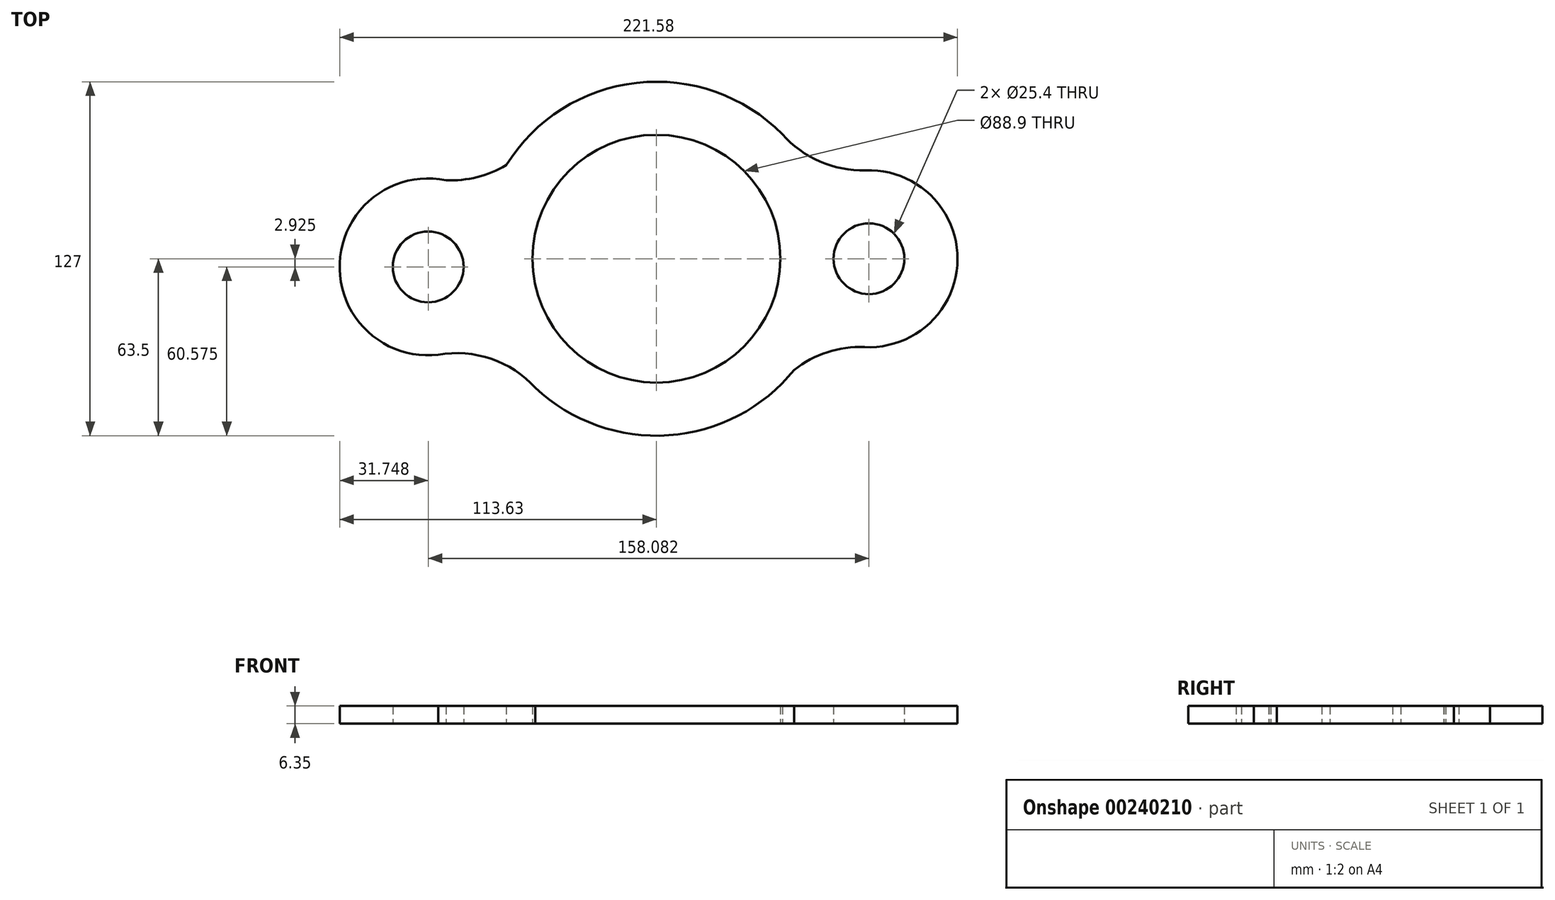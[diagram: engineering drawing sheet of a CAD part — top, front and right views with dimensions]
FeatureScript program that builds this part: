
annotation { "Feature Type Name" : "Feature", "Feature Type Description" : "" }
export const myFeature = defineFeature(function(context is Context, id is Id, definition is map)
    precondition{}
    {
        {
            var Q0;
            Q0=qCreatedBy(makeId("Top.planeOp"),FACE);
            var sketch = newSketch(context, id + "F0", { "sketchPlane" : qUnion([Q0])});
            skArc(sketch, "E0", {"start": v(-46.1, -43.67) * mm, "mid": v(2.51, -63.45) * mm, "end": v(49.4, -39.9) * mm});
            skCircle(sketch, "E1", {"center": v(0, 0) * mm, "radius": 44.45 * mm});
            skArc(sketch, "E2", {"start": v(74.6, -31.7) * mm, "mid": v(107.95, -0.17) * mm, "end": v(74.95, 31.73) * mm});
            skCircle(sketch, "E3", {"center": v(76.2, 0) * mm, "radius": 12.7 * mm});
            skArc(sketch, "E4", {"start": v(-75.5, 28.18) * mm, "mid": v(-113.6, -1.55) * mm, "end": v(-78.21, -34.46) * mm});
            skCircle(sketch, "E5", {"center": v(-81.88, -2.93) * mm, "radius": 12.7 * mm});
            skArc(sketch, "E6", {"start": v(-75.5, 28.18) * mm, "mid": v(-64.3, 29.25) * mm, "end": v(-53.91, 33.56) * mm});
            skArc(sketch, "E7", {"start": v(45.11, 44.69) * mm, "mid": v(58.58, 34.86) * mm, "end": v(74.95, 31.73) * mm});
            skArc(sketch, "E8", {"start": v(-43.43, -46.33) * mm, "mid": v(-59.3, -35.92) * mm, "end": v(-78.21, -34.46) * mm});
            skArc(sketch, "E9", {"start": v(74.6, -31.7) * mm, "mid": v(61.27, -33.54) * mm, "end": v(49.4, -39.9) * mm});
            skPoint(sketch, "E10.start.orphan", {"position": v(0, -44.45) * mm});
            skArc(sketch, "E11.trimOffspring", {"start": v(47.1, 42.59) * mm, "mid": v(-5.65, 63.25) * mm, "end": v(-53.91, 33.56) * mm});
            skLineSegment(sketch, "E12", {"start": v(0, 0) * mm, "end": v(76.2, 0) * mm});
            skSolve(sketch);
        }
        {
            var Q0;
            Q0=makeQuery(id+"F0.imprint","IMPRINT",FACE,{"disambiguationData":[TD([[makeQuery(id+"F0.imprint","IMPRINT",EDGE,{"derivedFrom":sQuery(id+"F0.wireOp",EDGE,"E1")}),-1.0]])]});
            extrude(context, id + "F1", {"entities" : qUnion([Q0]), "depth" : 6.35 * mm});
        }
    });
